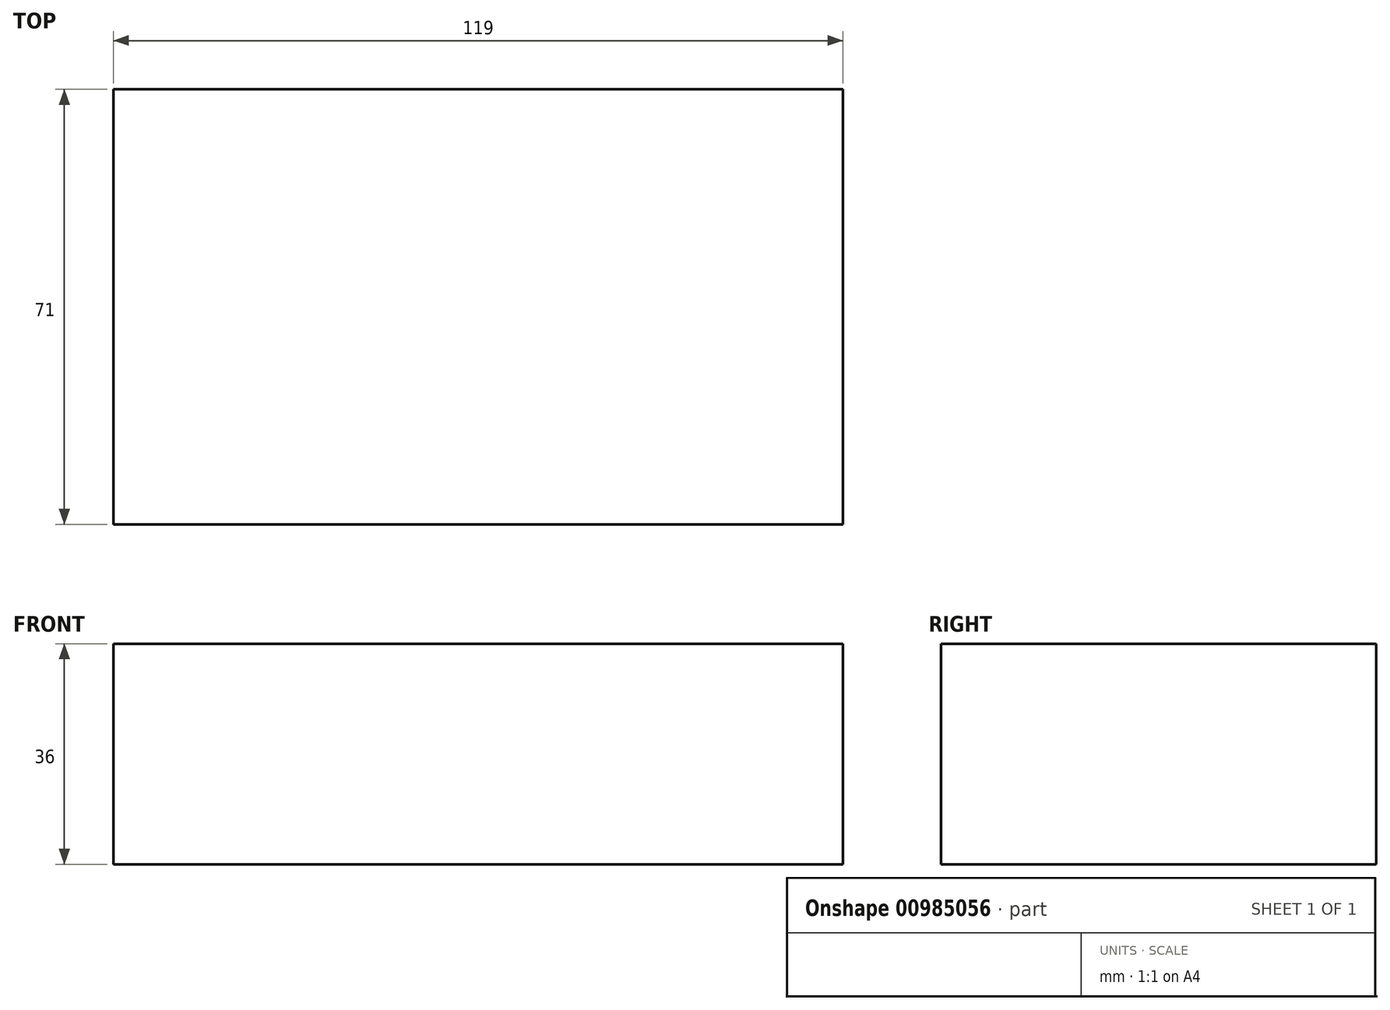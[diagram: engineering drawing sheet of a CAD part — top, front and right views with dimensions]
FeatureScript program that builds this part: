
annotation { "Feature Type Name" : "Feature", "Feature Type Description" : "" }
export const myFeature = defineFeature(function(context is Context, id is Id, definition is map)
    precondition{}
    {
        {
            var Q0;
            Q0=qCreatedBy(makeId("Top.planeOp"),FACE);
            var sketch = newSketch(context, id + "F0", { "sketchPlane" : qUnion([Q0])});
            skLineSegment(sketch, "E0.bottom", {"start": v(59.5, -35.5) * mm, "end": v(-59.5, -35.5) * mm});
            skLineSegment(sketch, "E0.top", {"start": v(59.5, 35.5) * mm, "end": v(-59.5, 35.5) * mm});
            skLineSegment(sketch, "E0.left", {"start": v(59.5, -35.5) * mm, "end": v(59.5, 35.5) * mm});
            skLineSegment(sketch, "E0.right", {"start": v(-59.5, -35.5) * mm, "end": v(-59.5, 35.5) * mm});
            skPoint(sketch, "E0.middle", {"position": v(0, 0) * mm});
            skSolve(sketch);
        }
        {
            var Q0;
            Q0=makeQuery(id+"F0.imprint","IMPRINT",FACE,{"disambiguationData":[TD([[makeQuery(id+"F0.imprint","IMPRINT",EDGE,{"derivedFrom":sQuery(id+"F0.wireOp",EDGE,"E0.bottom")}),-1.0]])]});
            extrude(context, id + "F1", {"entities" : qUnion([Q0]), "depth" : 36 * mm, "offsetDistance" : 25.4 * mm});
        }
    });
